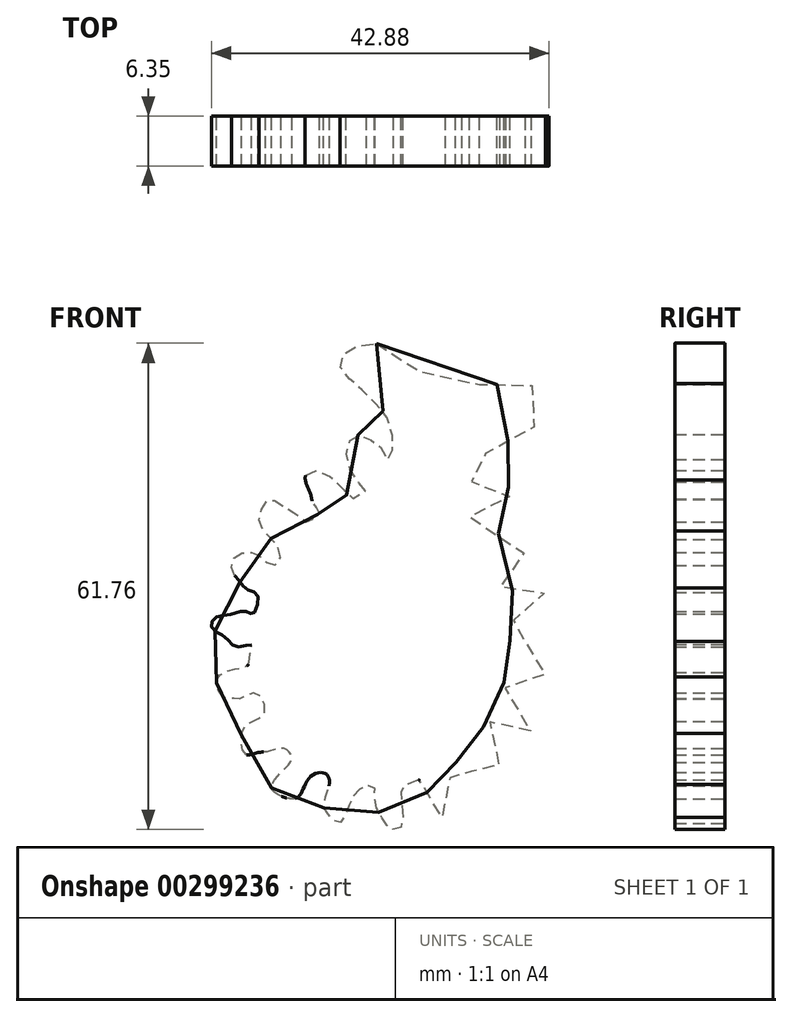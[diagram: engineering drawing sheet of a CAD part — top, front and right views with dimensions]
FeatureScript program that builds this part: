
annotation { "Feature Type Name" : "Feature", "Feature Type Description" : "" }
export const myFeature = defineFeature(function(context is Context, id is Id, definition is map)
    precondition{}
    {
        {
            var Q0;
            Q0=qCreatedBy(makeId("Front.planeOp"),FACE);
            var sketch = newSketch(context, id + "F0", { "sketchPlane" : qUnion([Q0])});
            skFitSpline(sketch, "E0", {"points": [v(23.33, 64.22) * mm, v(24.62, 63.39) * mm, v(26.55, 62) * mm, v(29.22, 60.44) * mm, v(31.9, 59.52) * mm, v(35.58, 59.06) * mm, v(39.27, 59.06) * mm, v(41.58, 59.15) * mm, v(43.14, 58.87) * mm, v(44.34, 57.67) * mm, v(44.71, 55.28) * mm, v(43.05, 53.43) * mm, v(40.65, 52.14) * mm, v(38.44, 50.94) * mm, v(35.86, 49.56) * mm, v(34.3, 48.36) * mm, v(34.57, 46.8) * mm, v(36.14, 46.8) * mm, v(38.44, 46.8) * mm, v(40, 46.06) * mm, v(40, 44.22) * mm, v(38.44, 43.39) * mm, v(36.32, 42.83) * mm, v(35.12, 42.1) * mm, v(35.68, 40.62) * mm, v(36.32, 39.42) * mm, v(38.07, 39.7) * mm, v(39.27, 40.34) * mm, v(40.65, 40.16) * mm, v(42.22, 38.69) * mm, v(41.4, 37.03) * mm, v(38.72, 36.1) * mm, v(38.81, 34.81) * mm, v(39.46, 32.7) * mm, v(41.4, 33.06) * mm, v(43.24, 33.06) * mm, v(45.17, 31.86) * mm, v(44.25, 29.93) * mm, v(41.67, 29.2) * mm, v(39.82, 28.55) * mm, v(40, 27.07) * mm, v(40.56, 26.33) * mm, v(42.22, 26.33) * mm, v(44.43, 24.95) * mm, v(45.17, 23.57) * mm, v(44.99, 22.46) * mm, v(43.24, 21.9) * mm, v(40.29, 22.37) * mm, v(39.55, 20.62) * mm, v(41.48, 18.78) * mm, v(42.77, 16.75) * mm, v(42.77, 14.9) * mm, v(40.65, 14.81) * mm, v(38.81, 15.46) * mm, v(37.98, 16.2) * mm, v(36.41, 14.63) * mm, v(37.61, 12.97) * mm, v(38.9, 10.57) * mm, v(38.72, 8.91) * mm, v(37.06, 8.27) * mm, v(35.5, 9.74) * mm, v(34.02, 10.94) * mm, v(32.73, 10.76) * mm, v(32.08, 9.83) * mm, v(33.1, 8.45) * mm, v(33.28, 6.52) * mm, v(32.64, 4.67) * mm, v(31.44, 4.03) * mm, v(30.7, 5.22) * mm, v(29.78, 7.07) * mm, v(28.86, 8.73) * mm, v(27.66, 8.36) * mm, v(26.64, 7.9) * mm, v(26.55, 5.5) * mm, v(26.37, 2.74) * mm, v(25.08, 2.64) * mm, v(24.25, 3.66) * mm, v(23.05, 6.05) * mm, v(23.05, 7.8) * mm, v(21.67, 7.9) * mm, v(20.2, 6.42) * mm, v(19.45, 4.49) * mm, v(18.53, 3.29) * mm, v(17.33, 4.21) * mm, v(16.6, 5.6) * mm, v(17.33, 8.17) * mm, v(16.87, 9.56) * mm, v(15.12, 9.37) * mm, v(13.83, 7.25) * mm, v(13, 6.42) * mm, v(11.25, 6.7) * mm, v(9.96, 7.9) * mm, v(12.08, 10.66) * mm, v(12.54, 11.86) * mm, v(11.53, 12.78) * mm, v(9.68, 12.41) * mm, v(8.12, 12.23) * mm, v(6.64, 12.05) * mm, v(6.18, 14.44) * mm, v(7, 15.92) * mm, v(9.13, 17.4) * mm, v(8.02, 19.79) * mm, v(6.09, 19.14) * mm, v(4.89, 19.14) * mm, v(3.97, 19.24) * mm, v(3.05, 20.62) * mm, v(3.32, 22) * mm, v(5.44, 22.92) * mm, v(6.92, 23.3) * mm, v(7.29, 24.86) * mm, v(7.38, 25.96) * mm, v(5.53, 25.69) * mm, v(4.15, 26.89) * mm, v(2.5, 28) * mm, v(2.68, 29.28) * mm, v(4.61, 29.74) * mm, v(5.72, 30.11) * mm, v(6.92, 30.11) * mm, v(7.65, 29.93) * mm, v(8.2, 32.23) * mm, v(6.92, 32.97) * mm, v(5.72, 34.26) * mm, v(4.89, 35.64) * mm, v(5.53, 37.3) * mm, v(7.29, 37.67) * mm, v(8.48, 37.21) * mm, v(10.14, 36.01) * mm, v(11.16, 37.12) * mm, v(9.96, 39.42) * mm, v(8.48, 41.27) * mm, v(8.85, 43.48) * mm, v(9.96, 44.4) * mm, v(11.9, 43.3) * mm, v(13.65, 42.19) * mm, v(14.3, 41.54) * mm, v(15.4, 42.1) * mm, v(16.04, 43.02) * mm, v(15.4, 43.66) * mm, v(14.94, 45.14) * mm, v(14.3, 46.8) * mm, v(14.48, 47.72) * mm, v(15.67, 48.09) * mm, v(16.96, 47.63) * mm, v(19, 45.88) * mm, v(20, 44.5) * mm, v(21.3, 45.14) * mm, v(22.03, 45.7) * mm, v(21.2, 46.43) * mm, v(20.1, 47.9) * mm, v(19.55, 49.93) * mm, v(19.55, 51.04) * mm, v(20.47, 52.51) * mm, v(21.11, 52.6) * mm, v(22.31, 52.14) * mm, v(23.05, 51.68) * mm, v(23.97, 50.85) * mm, v(24.7, 49.47) * mm, v(25.17, 50.12) * mm, v(25.45, 51.04) * mm, v(25.26, 52.97) * mm, v(24.34, 55.37) * mm, v(22.59, 57.21) * mm, v(20.74, 59.06) * mm, v(19.36, 60.16) * mm, v(18.72, 61.45) * mm, v(19.08, 62.84) * mm, v(20.47, 63.76) * mm, v(23.33, 64.22) * mm]});
            skSolve(sketch);
        }
        {
            var Q0;
            Q0=makeQuery(id+"F0.imprint","IMPRINT",FACE,{"disambiguationData":[TD([[makeQuery(id+"F0.imprint","IMPRINT",EDGE,{"derivedFrom":sQuery(id+"F0.wireOp",EDGE,"E0")}),-1.0]])]});
            extrude(context, id + "F1", {"entities" : qUnion([Q0]), "depth" : 6.35 * mm});
        }
    });
